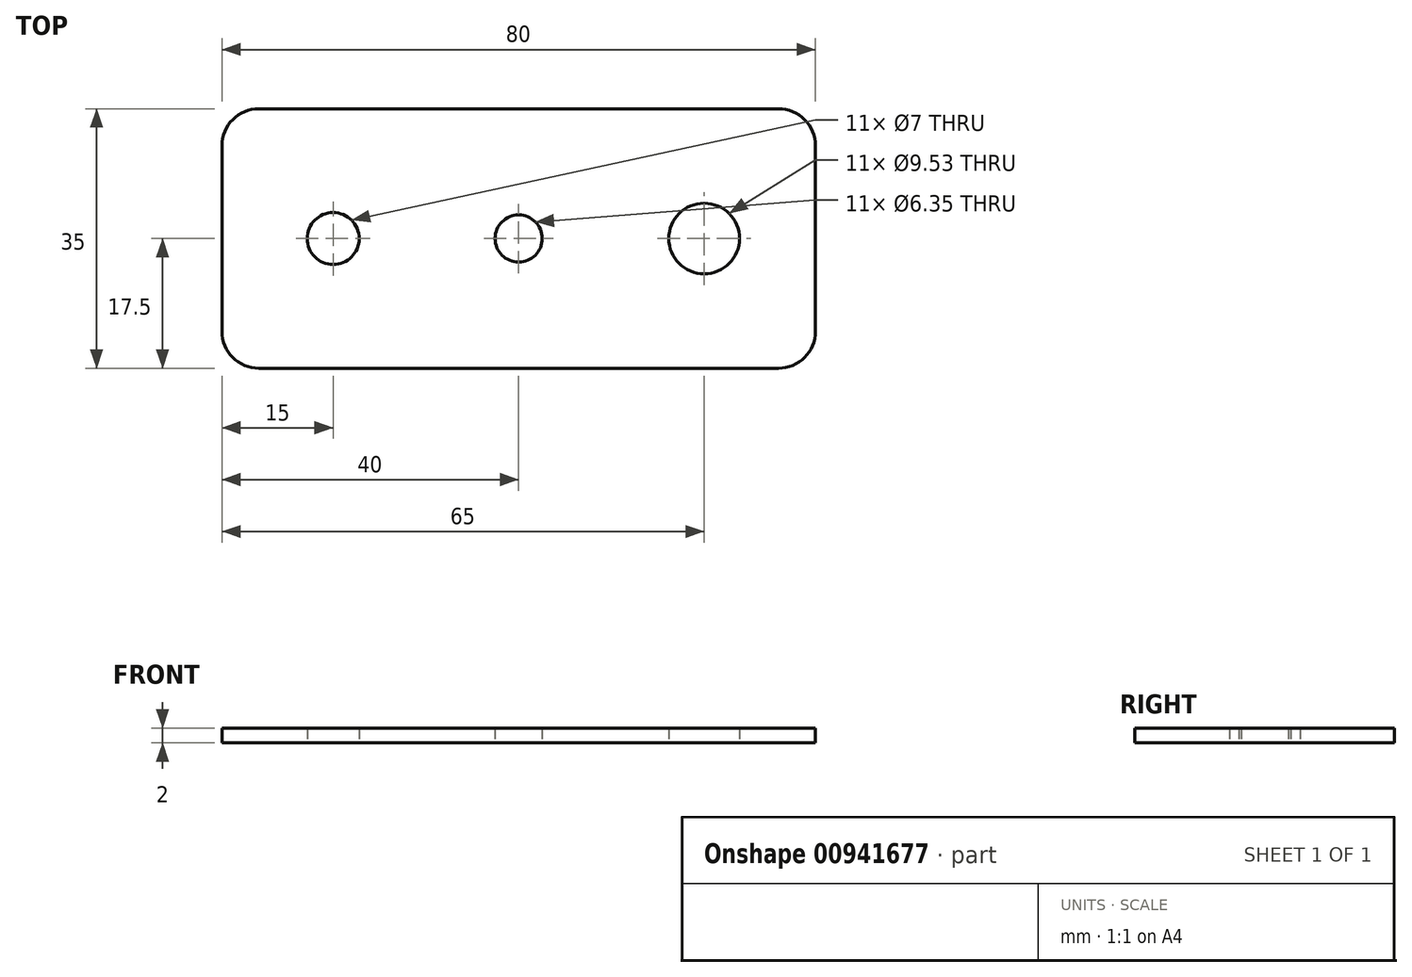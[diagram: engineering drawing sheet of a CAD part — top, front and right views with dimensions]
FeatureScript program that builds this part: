
annotation { "Feature Type Name" : "Feature", "Feature Type Description" : "" }
export const myFeature = defineFeature(function(context is Context, id is Id, definition is map)
    precondition{}
    {
        {
            var Q0;
            Q0=qCreatedBy(makeId("Top.planeOp"),FACE);
            var sketch = newSketch(context, id + "F0", { "sketchPlane" : qUnion([Q0])});
            skLineSegment(sketch, "E0.bottom", {"start": v(35, 17.5) * mm, "end": v(-35, 17.5) * mm});
            skLineSegment(sketch, "E0.top", {"start": v(35, -17.5) * mm, "end": v(-35, -17.5) * mm});
            skLineSegment(sketch, "E0.left", {"start": v(40, 12.5) * mm, "end": v(40, -12.5) * mm});
            skLineSegment(sketch, "E0.right", {"start": v(-40, 12.5) * mm, "end": v(-40, -12.5) * mm});
            skPoint(sketch, "E0.middle", {"position": v(0, 0) * mm});
            skCircle(sketch, "E1", {"center": v(-25, 0) * mm, "radius": 3.5 * mm});
            skCircle(sketch, "E2", {"center": v(25, 0) * mm, "radius": 4.76 * mm});
            skCircle(sketch, "E3", {"center": v(0, 0) * mm, "radius": 3.17 * mm});
            skPoint(sketch, "E4.visualSharp", {"position": v(-40, 17.5) * mm});
            skArc(sketch, "E4.filletArc", {"start": v(-35, 17.5) * mm, "mid": v(-38.54, 16.04) * mm, "end": v(-40, 12.5) * mm});
            skPoint(sketch, "E5.visualSharp", {"position": v(-40, -17.5) * mm});
            skArc(sketch, "E5.filletArc", {"start": v(-40, -12.5) * mm, "mid": v(-38.54, -16.04) * mm, "end": v(-35, -17.5) * mm});
            skPoint(sketch, "E6.visualSharp", {"position": v(40, 17.5) * mm});
            skArc(sketch, "E6.filletArc", {"start": v(40, 12.5) * mm, "mid": v(38.54, 16.04) * mm, "end": v(35, 17.5) * mm});
            skPoint(sketch, "E7.visualSharp", {"position": v(40, -17.5) * mm});
            skArc(sketch, "E7.filletArc", {"start": v(35, -17.5) * mm, "mid": v(38.54, -16.04) * mm, "end": v(40, -12.5) * mm});
            skSolve(sketch);
        }
        {
            var Q0;
            Q0=makeQuery(id+"F0.imprint","IMPRINT",FACE,{"disambiguationData":[TD([[makeQuery(id+"F0.imprint","IMPRINT",EDGE,{"derivedFrom":sQuery(id+"F0.wireOp",EDGE,"E0.bottom")}),1.0]])]});
            extrude(context, id + "F1", {"entities" : qUnion([Q0]), "depth" : 2 * mm, "offsetDistance" : 25 * mm});
        }
    });
